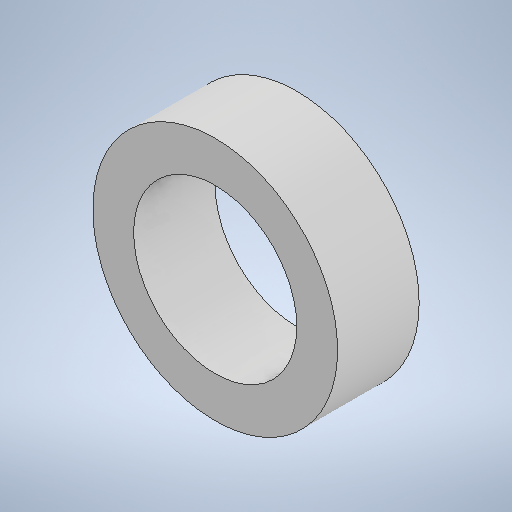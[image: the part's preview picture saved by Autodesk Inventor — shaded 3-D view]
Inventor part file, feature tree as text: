
AUTODESK INVENTOR PART (.ipt)
format: ipt  version: 2025.3 (Build 293356000, 356)  size: 210,432 bytes
history: native  units: in
note: dims shown in document units (in); Inventor stores cm internally (conversion verified against a paired STEP export)
features: extrude x1, sketch x1
ambient origin geometry x8: Origin, YZ Plane, XZ Plane, XY Plane, X Axis, Y Axis, Z Axis, Center Point
bodies: Solid1 (feature_tree)
feature tree (2):
  extrude  "Extrusion1"  Depth=0.1181in
  sketch  "Sketch1"  dims[d0=0.2362in d1=0.3543in d2=0.1181in d3=0.0in]
